# Revit family: P560256-031
name_source: partatom
category: Lighting Fixtures
units: mm (PartAtom-declared; Revit-internal decimal feet)

## family parameters
Cut with Voids When Loaded = No
Host = Face
Light Source = Yes
OmniClass Number = 23.80.70.11.14.17
OmniClass Title = Direct/Indirect
Part Type = Normal
Room Calculation Point = No
Round Connector Dimension = Use Diameter
Shared = Yes

## types (1)
- P560256-031
    Apparent Load = 60 VA
    Assembly Code = D5020200
    Color Filter = 16777215
    Connector Description = Lighting Connector
    Default Elevation = 48 "
    Description = Watch Hill Collection One-Light Textured Black and Clear Seeded Glass Farmhouse Style Medium Outdoor Wall Lantern
    Dimming Lamp Color Temperature Shift = <None>
    Features = Application: Incorporate a timeless style inspired by Victorian-era gaslight fittings with the Watch Hill Collection 1-Light Textured Black Clear Seeded Glass Farmhouse Outdoor Medium Wall Lantern Light ideal for any covered porch, patio, deck, entryway, bedroom, foyer, barn, or garage.
Styles: Perfect for transitional and farmhouse style settings.
Finish: The elongated cage design highlighted by gracefully curving slender arms is coated in a classic textured black finish.
Materials: Constructed from aluminum to ensure a long product lifespan.
Glass/Shades: The frame cradles a seeded glass shade that complements a variety of home styles.
Bulbs: For ideal illumination, use 1 medium base bulb that is sold separately (60w max - LED/CFL/incandescent). Compatible with dimmable bulbs.
Dimensions: Measures 7-1/2-inch diameter by 17-inch height.
Certifications: cCSAus wet location listed.
Pairs With: Pairs with a variety of Progress Lighting fixtures.
Warranty: Our 1-Year Limited Warranty guarantees your complete satisfaction with your purchase and includes professional after-sales customer service support.
    Fixture distribution = Direct
    Glass = Paint - Hubbell - White Texture
    Gold = Hubbell - Gold
    Housing Material = Paint - Hubbell - Textured Camera Black
    Lamp = Incandescent
    Load Classification = Lighting
    Manufacturer = Progress Lighting
    Model = P560256-031
    Photometric Web File = generic
    Power Factor = 1
    Product Documentation Link = https://hubbellcdn.com
    Product Link = https://www.hubbell.com
    Tilt Angle = 60.00°
    URL = https://www.hubbell.com
    Voltage = 120 V
    Warranty = 1 year Warranty
    Wattage Comments = 60W
    Watts = 60 W

## geometry (parser evidence)
native form markers: Sweep x1
no freeform markers — native parametric forms only
